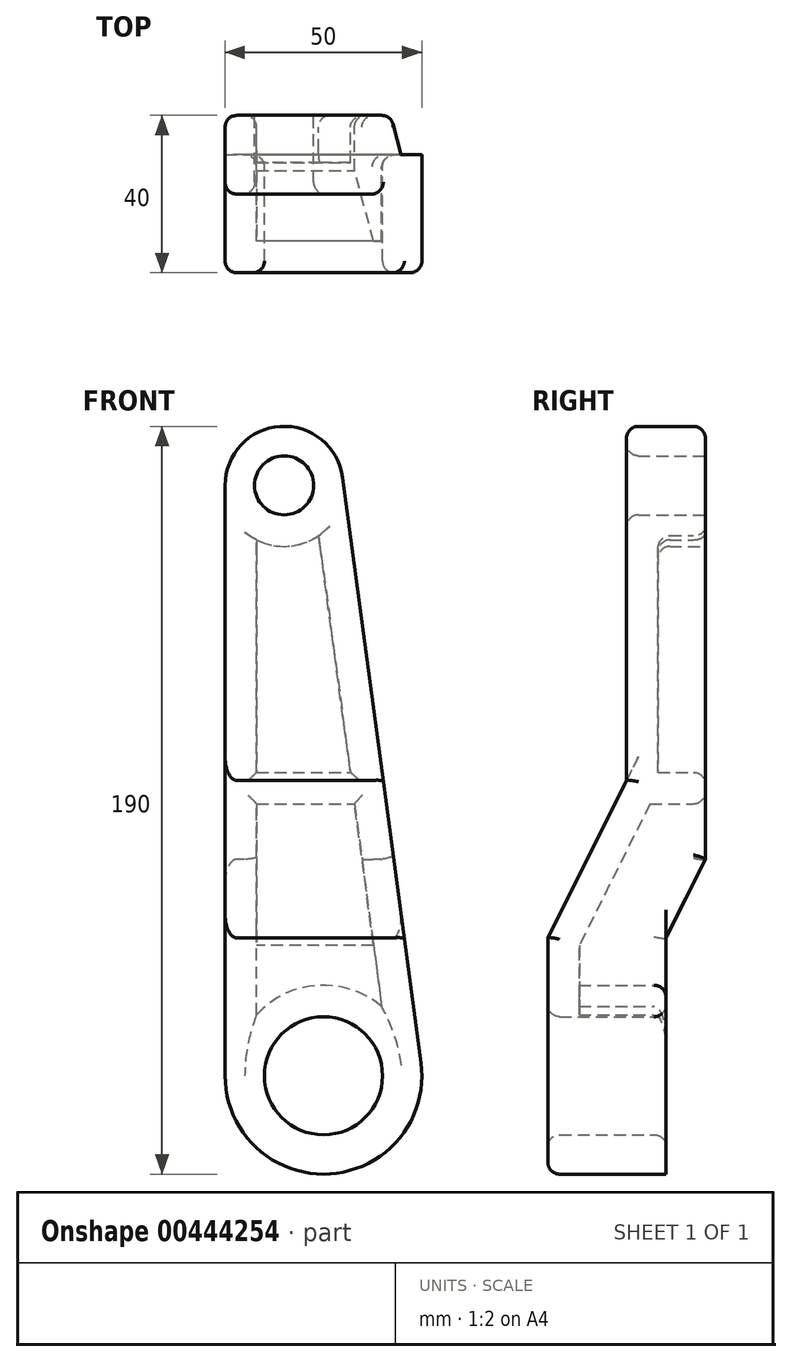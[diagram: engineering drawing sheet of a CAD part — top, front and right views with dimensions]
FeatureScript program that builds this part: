
annotation { "Feature Type Name" : "Feature", "Feature Type Description" : "" }
export const myFeature = defineFeature(function(context is Context, id is Id, definition is map)
    precondition{}
    {
        {
            var Q0;
            Q0=qCreatedBy(makeId("Front.planeOp"),FACE);
            var sketch = newSketch(context, id + "F0", { "sketchPlane" : qUnion([Q0])});
            skCircle(sketch, "E0", {"center": v(0, 0) * mm, "radius": 25 * mm});
            skLineSegment(sketch, "E1", {"start": v(-25, 0) * mm, "end": v(-25, 150) * mm});
            skCircle(sketch, "E2", {"center": v(-10, 150) * mm, "radius": 15 * mm});
            skLineSegment(sketch, "E3", {"start": v(4.87, 152) * mm, "end": v(24.78, 3.32) * mm});
            skSolve(sketch);
        }
        {
            var Q0;
            Q0 = qSketchRegion(id + "F0", true);
            extrude(context, id + "F1", {"entities" : qUnion([Q0]), "depth" : 40 * mm});
        }
        {
            var Q0;
            Q0=makeQuery(id+"F1.opExtrude","SWEPT_FACE",FACE,{"disambiguationData":[OSD([sQuery(id+"F0.wireOp",EDGE,"E1")])]});
            var sketch = newSketch(context, id + "F2", { "sketchPlane" : qUnion([Q0])});
            skLineSegment(sketch, "E4", {"start": v(0, 55) * mm, "end": v(0, -25.94) * mm});
            skLineSegment(sketch, "E5", {"start": v(10, -25.94) * mm, "end": v(10, 35) * mm});
            skLineSegment(sketch, "E6", {"start": v(10, 35) * mm, "end": v(0, 55) * mm});
            skLineSegment(sketch, "E7", {"start": v(40, 35) * mm, "end": v(40, 165.97) * mm});
            skLineSegment(sketch, "E8", {"start": v(20, 165.97) * mm, "end": v(20, 75) * mm});
            skLineSegment(sketch, "E9", {"start": v(20, 75) * mm, "end": v(40, 35) * mm});
            skLineSegment(sketch, "E10", {"start": v(0, -25.94) * mm, "end": v(10, -25.94) * mm});
            skLineSegment(sketch, "E11", {"start": v(20, 165.97) * mm, "end": v(40, 165.97) * mm});
            skSolve(sketch);
        }
        {
            var Q0;
            Q0 = qSketchRegion(id + "F2", true);
            extrude(context, id + "F3", {"entities" : qUnion([Q0]), "operationType" : NewBodyOperationType.REMOVE, "endBound" : BoundingType.THROUGH_ALL, "oppositeDirection" : true, "depth" : 25 * mm});
        }
        {
            var Q0;
            Q0=makeQuery(id+"F1.opExtrude","CAP_FACE",FACE,{"disambiguationData":[OSD([sQuery(id+"F0.wireOp",EDGE,"E0"),sQuery(id+"F0.wireOp",EDGE,"E1"),sQuery(id+"F0.wireOp",EDGE,"E2"),sQuery(id+"F0.wireOp",EDGE,"E3")])],"isStart":true});
            var sketch = newSketch(context, id + "F4", { "sketchPlane" : qUnion([Q0])});
            skCircle(sketch, "E12", {"center": v(10, 150) * mm, "radius": 7.5 * mm});
            skCircle(sketch, "E13", {"center": v(0, 0) * mm, "radius": 15 * mm});
            skSolve(sketch);
        }
        {
            var Q0;
            Q0 = qSketchRegion(id + "F4", true);
            extrude(context, id + "F5", {"entities" : qUnion([Q0]), "operationType" : NewBodyOperationType.REMOVE, "endBound" : BoundingType.THROUGH_ALL, "oppositeDirection" : true, "depth" : 25 * mm});
        }
        {
            var Q0;
            Q0=makeQuery(id+"F1.opExtrude","CAP_FACE",FACE,{"disambiguationData":[OSD([sQuery(id+"F0.wireOp",EDGE,"E0"),sQuery(id+"F0.wireOp",EDGE,"E1"),sQuery(id+"F0.wireOp",EDGE,"E2"),sQuery(id+"F0.wireOp",EDGE,"E3")])],"isStart":true});
            var Q1;
            Q1=makeQuery(id+"F3.boolean.opBoolean","COPY",FACE,{"derivedFrom":makeQuery(id+"F3.opExtrude","SWEPT_FACE",FACE,{"disambiguationData":[OSD([sQuery(id+"F2.wireOp",EDGE,"E6")])]})});
            var Q2;
            Q2=makeQuery(id+"F3.boolean.opBoolean","COPY",FACE,{"derivedFrom":makeQuery(id+"F3.opExtrude","SWEPT_FACE",FACE,{"disambiguationData":[OSD([sQuery(id+"F2.wireOp",EDGE,"E5")])]})});
            shell(context, id + "F6", {"entities" : qUnion([Q0, Q1, Q2]), "thickness" : 8 * mm});
        }
        {
            var Q0;
            Q0=makeQuery(id+"F1.opExtrude","CAP_FACE",FACE,{"disambiguationData":[OSD([sQuery(id+"F0.wireOp",EDGE,"E0"),sQuery(id+"F0.wireOp",EDGE,"E1"),sQuery(id+"F0.wireOp",EDGE,"E2"),sQuery(id+"F0.wireOp",EDGE,"E3")])],"isStart":true});
            var sketch = newSketch(context, id + "F7", { "sketchPlane" : qUnion([Q0])});
            skLineSegment(sketch, "E14", {"start": v(-6.82, 77.11) * mm, "end": v(17, 77.11) * mm});
            skLineSegment(sketch, "E15", {"start": v(-7.9, 69.11) * mm, "end": v(17, 69.11) * mm});
            skLineSegment(sketch, "E16.0", {"start": v(1.23, 137.22) * mm, "end": v(-9.79, 55) * mm});
            skLineSegment(sketch, "E17.0", {"start": v(17, 55) * mm, "end": v(17, 136.17) * mm});
            skSolve(sketch);
        }
        {
            var Q0;
            Q0 = qSketchRegion(id + "F7", true);
            extrude(context, id + "F8", {"entities" : qUnion([Q0]), "operationType" : NewBodyOperationType.ADD, "endBound" : BoundingType.UP_TO_NEXT, "oppositeDirection" : true, "depth" : 25 * mm});
        }
        {
            var Q0;
            Q0=makeQuery(id+"F1.opExtrude","CAP_EDGE",EDGE,{"disambiguationData":[OSD([sQuery(id+"F0.wireOp",EDGE,"E2")])],"isStart":true});
            var Q1;
            Q1=makeQuery(id+"F3.boolean.opBoolean","INTERSECT",EDGE,{"derivedFrom":[makeQuery(id+"F1.opExtrude","SWEPT_FACE",FACE,{"disambiguationData":[OSD([sQuery(id+"F0.wireOp",EDGE,"E3")])]}),makeQuery(id+"F3.opExtrude","SWEPT_FACE",FACE,{"disambiguationData":[OSD([sQuery(id+"F2.wireOp",EDGE,"E6")])]})]});
            var Q2;
            Q2=makeQuery(id+"F3.boolean.opBoolean","COPY",EDGE,{"derivedFrom":makeQuery(id+"F3.opExtrude","CAP_EDGE",EDGE,{"disambiguationData":[OSD([sQuery(id+"F2.wireOp",EDGE,"E6")])],"isStart":true})});
            var Q3;
            Q3=makeQuery(id+"F3.boolean.opBoolean","COPY",EDGE,{"derivedFrom":makeQuery(id+"F3.opExtrude","CAP_EDGE",EDGE,{"disambiguationData":[OSD([sQuery(id+"F2.wireOp",EDGE,"E5")])],"isStart":true})});
            var Q4;
            Q4=makeQuery(id+"F3.boolean.opBoolean","INTERSECT",EDGE,{"derivedFrom":[makeQuery(id+"F1.opExtrude","SWEPT_FACE",FACE,{"disambiguationData":[OSD([sQuery(id+"F0.wireOp",EDGE,"E2")])]}),makeQuery(id+"F3.opExtrude","SWEPT_FACE",FACE,{"disambiguationData":[OSD([sQuery(id+"F2.wireOp",EDGE,"E8")])]})]});
            var Q5;
            Q5=makeQuery(id+"F3.boolean.opBoolean","INTERSECT",EDGE,{"derivedFrom":[makeQuery(id+"F1.opExtrude","SWEPT_FACE",FACE,{"disambiguationData":[OSD([sQuery(id+"F0.wireOp",EDGE,"E3")])]}),makeQuery(id+"F3.opExtrude","SWEPT_FACE",FACE,{"disambiguationData":[OSD([sQuery(id+"F2.wireOp",EDGE,"E9")])]})]});
            var Q6;
            Q6=makeQuery(id+"F3.boolean.opBoolean","COPY",EDGE,{"derivedFrom":makeQuery(id+"F3.opExtrude","CAP_EDGE",EDGE,{"disambiguationData":[OSD([sQuery(id+"F2.wireOp",EDGE,"E9")])],"isStart":true})});
            var Q7;
            Q7=makeQuery(id+"F1.opExtrude","CAP_EDGE",EDGE,{"disambiguationData":[OSD([sQuery(id+"F0.wireOp",EDGE,"E1")])],"isStart":false});
            var Q8;
            Q8=makeQuery(id+"F5.boolean.opBoolean","COPY",EDGE,{"derivedFrom":makeQuery(id+"F5.opExtrude","CAP_EDGE",EDGE,{"disambiguationData":[OSD([sQuery(id+"F4.wireOp",EDGE,"E12")])],"isStart":true})});
            var Q9;
            Q9=makeQuery(id+"F6.opShell","OFFSET_EDGE",EDGE,{"disambiguationData":[OSD([sQuery(id+"F4.wireOp",EDGE,"E12")])]});
            var Q10;
            {var subQ1=sQuery(id+"F0.wireOp",EDGE,"E3");Q10=makeQuery(id+"F8.boolean.opBoolean","SPLIT",EDGE,{"disambiguationData":[TD([makeQuery(id+"F6.opShell","OFFSET_FACE",FACE,{"disambiguationData":[OSD([sQuery(id+"F4.wireOp",EDGE,"E12")])]})])],"derivedFrom":makeQuery(id+"F6.opShell","OFFSET_EDGE",EDGE,{"disambiguationData":[OSD([subQ1]),TDD([makeQuery(id+"F1.opExtrude","CAP_EDGE",EDGE,{"disambiguationData":[OSD([subQ1])],"isStart":true})])]})});}
            var Q11;
            Q11=makeQuery(id+"F8.opExtrude","CAP_EDGE",EDGE,{"disambiguationData":[OSD([sQuery(id+"F7.wireOp",EDGE,"E14")])],"isStart":true});
            var Q12;
            {var subQ1=sQuery(id+"F0.wireOp",EDGE,"E1");Q12=makeQuery(id+"F8.boolean.opBoolean","SPLIT",EDGE,{"disambiguationData":[TD([makeQuery(id+"F6.opShell","OFFSET_FACE",FACE,{"disambiguationData":[OSD([sQuery(id+"F4.wireOp",EDGE,"E12")])]})])],"derivedFrom":makeQuery(id+"F6.opShell","OFFSET_EDGE",EDGE,{"disambiguationData":[OSD([subQ1]),TDD([makeQuery(id+"F1.opExtrude","CAP_EDGE",EDGE,{"disambiguationData":[OSD([subQ1])],"isStart":true})])]})});}
            var Q13;
            Q13=makeQuery(id+"F8.opExtrude","CAP_EDGE",EDGE,{"disambiguationData":[OSD([sQuery(id+"F7.wireOp",EDGE,"E15")])],"isStart":true});
            var Q14;
            {var subQ1=sQuery(id+"F0.wireOp",EDGE,"E3");Q14=makeQuery(id+"F8.boolean.opBoolean","SPLIT",EDGE,{"disambiguationData":[TD([makeQuery(id+"F6.opShell","OFFSET_FACE",FACE,{"disambiguationData":[OSD([sQuery(id+"F2.wireOp",EDGE,"E6")])]})])],"derivedFrom":makeQuery(id+"F6.opShell","OFFSET_EDGE",EDGE,{"disambiguationData":[OSD([subQ1]),TDD([makeQuery(id+"F1.opExtrude","CAP_EDGE",EDGE,{"disambiguationData":[OSD([subQ1])],"isStart":true})])]})});}
            var Q15;
            Q15=makeQuery(id+"F6.opShell","OFFSET_EDGE",EDGE,{"disambiguationData":[OSD([sQuery(id+"F0.wireOp",EDGE,"E3"),sQuery(id+"F2.wireOp",EDGE,"E6")])]});
            var Q16;
            {var subQ0=sQuery(id+"F0.wireOp",EDGE,"E1");Q16=makeQuery(id+"F8.boolean.opBoolean","SPLIT",EDGE,{"disambiguationData":[TD([makeQuery(id+"F3.boolean.opBoolean","COPY",FACE,{"derivedFrom":makeQuery(id+"F3.opExtrude","SWEPT_FACE",FACE,{"disambiguationData":[OSD([sQuery(id+"F2.wireOp",EDGE,"E6")])]})})])],"derivedFrom":makeQuery(id+"F6.opShell","OFFSET_EDGE",EDGE,{"disambiguationData":[OSD([subQ0]),TDD([makeQuery(id+"F1.opExtrude","CAP_EDGE",EDGE,{"disambiguationData":[OSD([subQ0])],"isStart":true})])]})});}
            var Q17;
            Q17=makeQuery(id+"F6.opShell","OFFSET_EDGE",EDGE,{"disambiguationData":[OSD([sQuery(id+"F2.wireOp",EDGE,"E6")])]});
            var Q18;
            Q18=makeQuery(id+"F6.opShell","OFFSET_EDGE",EDGE,{"disambiguationData":[OSD([sQuery(id+"F2.wireOp",EDGE,"E5")])]});
            var Q19;
            Q19=makeQuery(id+"F6.opShell","OFFSET_EDGE",EDGE,{"disambiguationData":[OSD([sQuery(id+"F2.wireOp",EDGE,"E5"),sQuery(id+"F4.wireOp",EDGE,"E13")])]});
            var Q20;
            Q20=makeQuery(id+"F6.opShell","OFFSET_EDGE",EDGE,{"disambiguationData":[OSD([sQuery(id+"F0.wireOp",EDGE,"E3"),sQuery(id+"F2.wireOp",EDGE,"E5")])]});
            var Q21;
            Q21=makeQuery(id+"F5.boolean.opBoolean","INTERSECT",EDGE,{"derivedFrom":[makeQuery(id+"F3.boolean.opBoolean","COPY",FACE,{"derivedFrom":makeQuery(id+"F3.opExtrude","SWEPT_FACE",FACE,{"disambiguationData":[OSD([sQuery(id+"F2.wireOp",EDGE,"E5")])]})}),makeQuery(id+"F5.opExtrude","SWEPT_FACE",FACE,{"disambiguationData":[OSD([sQuery(id+"F4.wireOp",EDGE,"E13")])]})]});
            var Q22;
            Q22=makeQuery(id+"F5.boolean.opBoolean","INTERSECT",EDGE,{"derivedFrom":[makeQuery(id+"F3.boolean.opBoolean","COPY",FACE,{"derivedFrom":makeQuery(id+"F3.opExtrude","SWEPT_FACE",FACE,{"disambiguationData":[OSD([sQuery(id+"F2.wireOp",EDGE,"E8")])]})}),makeQuery(id+"F5.opExtrude","SWEPT_FACE",FACE,{"disambiguationData":[OSD([sQuery(id+"F4.wireOp",EDGE,"E12")])]})]});
            var Q23;
            Q23=makeQuery(id+"F5.boolean.opBoolean","INTERSECT",EDGE,{"derivedFrom":[makeQuery(id+"F1.opExtrude","CAP_FACE",FACE,{"disambiguationData":[OSD([sQuery(id+"F0.wireOp",EDGE,"E0"),sQuery(id+"F0.wireOp",EDGE,"E1"),sQuery(id+"F0.wireOp",EDGE,"E2"),sQuery(id+"F0.wireOp",EDGE,"E3")])],"isStart":false}),makeQuery(id+"F5.opExtrude","SWEPT_FACE",FACE,{"disambiguationData":[OSD([sQuery(id+"F4.wireOp",EDGE,"E13")])]})]});
            fillet(context, id + "F9", {"entities" : qUnion([Q0, Q1, Q2, Q3, Q4, Q5, Q6, Q7, Q8, Q9, Q10, Q11, Q12, Q13, Q14, Q15, Q16, Q17, Q18, Q19, Q20, Q21, Q22, Q23]), "radius" : 3 * mm, "tangentPropagation" : true, "allowEdgeOverflow" : false});
        }
    });
